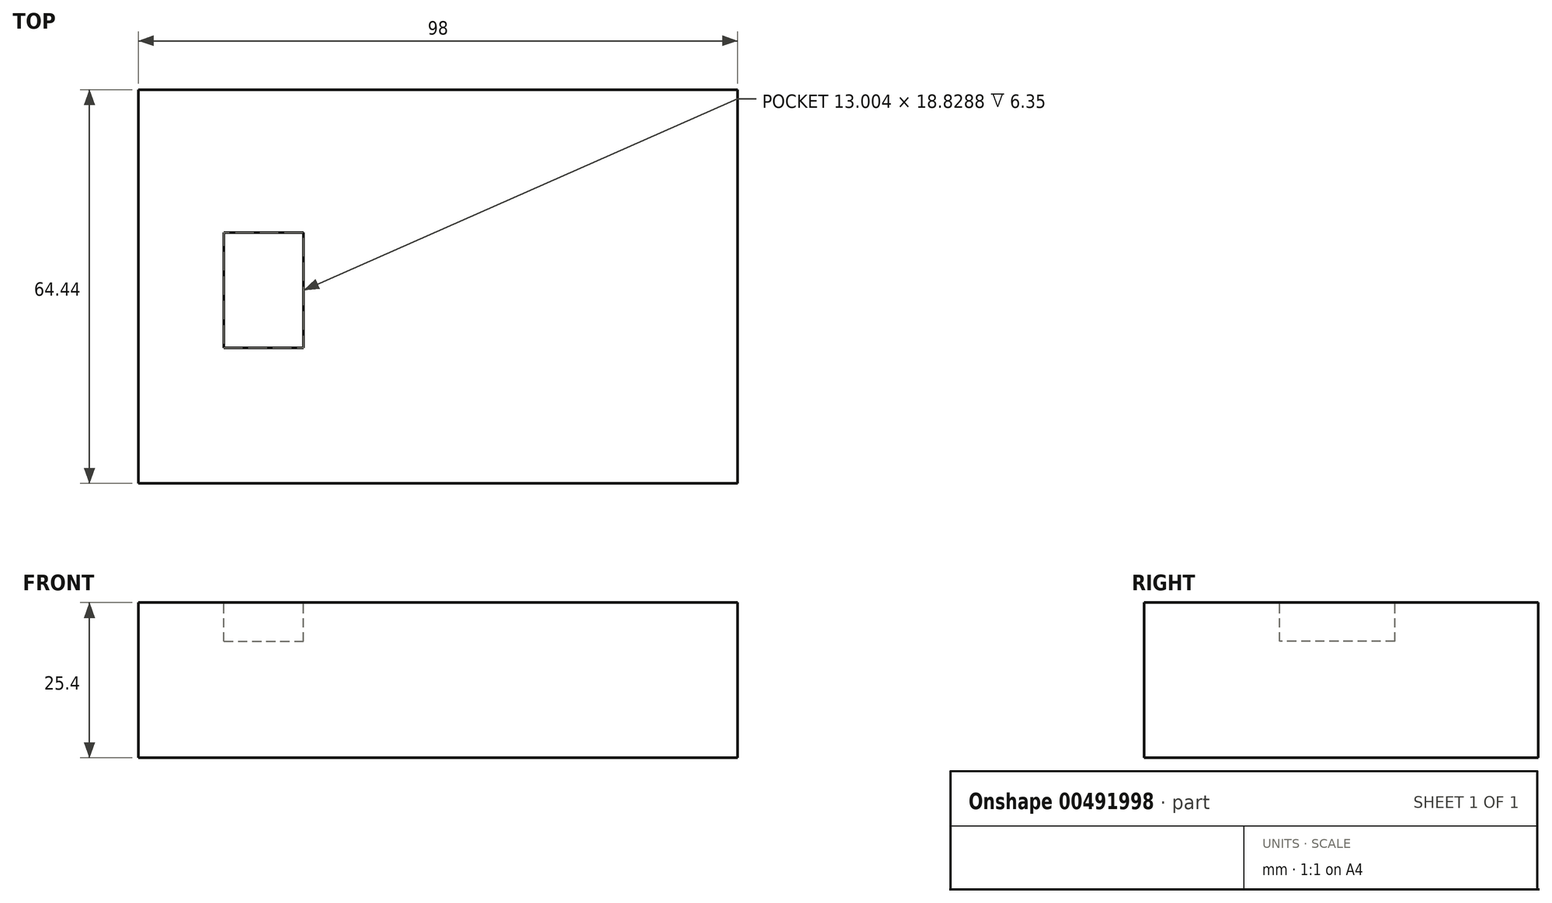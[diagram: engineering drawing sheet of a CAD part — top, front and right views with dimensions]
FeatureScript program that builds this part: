
annotation { "Feature Type Name" : "Feature", "Feature Type Description" : "" }
export const myFeature = defineFeature(function(context is Context, id is Id, definition is map)
    precondition{}
    {
        {
            var Q0;
            Q0=qCreatedBy(makeId("Top.planeOp"),FACE);
            var sketch = newSketch(context, id + "F0", { "sketchPlane" : qUnion([Q0])});
            skLineSegment(sketch, "E0.bottom", {"start": v(-49, -32.22) * mm, "end": v(49, -32.22) * mm});
            skLineSegment(sketch, "E0.top", {"start": v(-49, 32.22) * mm, "end": v(49, 32.22) * mm});
            skLineSegment(sketch, "E0.left", {"start": v(-49, -32.22) * mm, "end": v(-49, 32.22) * mm});
            skLineSegment(sketch, "E0.right", {"start": v(49, -32.22) * mm, "end": v(49, 32.22) * mm});
            skPoint(sketch, "E0.middle", {"position": v(0, 0) * mm});
            skLineSegment(sketch, "E1.bottom", {"start": v(25, 32.22) * mm, "end": v(-25, 32.22) * mm});
            skLineSegment(sketch, "E1.top", {"start": v(25, 32.22) * mm, "end": v(-25, 32.22) * mm});
            skLineSegment(sketch, "E1.left", {"start": v(25, 32.22) * mm, "end": v(25, 32.22) * mm});
            skLineSegment(sketch, "E1.right", {"start": v(-25, 32.22) * mm, "end": v(-25, 32.22) * mm});
            skPoint(sketch, "E1.middle", {"position": v(0, 32.22) * mm});
            skSolve(sketch);
        }
        {
            var Q0;
            Q0=makeQuery(id+"F0.imprint","IMPRINT",FACE,{"disambiguationData":[TD([[makeQuery(id+"F0.imprint","IMPRINT",EDGE,{"derivedFrom":sQuery(id+"F0.wireOp",EDGE,"E0.bottom")}),1.0]])]});
            extrude(context, id + "F1", {"entities" : qUnion([Q0]), "depth" : 25.4 * mm});
        }
        {
            var Q0;
            Q0=makeQuery(id+"F1.opExtrude","CAP_FACE",FACE,{"disambiguationData":[OSD([sQuery(id+"F0.wireOp",EDGE,"E0.bottom"),sQuery(id+"F0.wireOp",EDGE,"E0.top"),sQuery(id+"F0.wireOp",EDGE,"E0.left"),sQuery(id+"F0.wireOp",EDGE,"E0.right"),sQuery(id+"F0.wireOp",EDGE,"E1.top")])],"isStart":false});
            var sketch = newSketch(context, id + "F2", { "sketchPlane" : qUnion([Q0])});
            skLineSegment(sketch, "E2.bottom", {"start": v(-35, 8.8) * mm, "end": v(-22, 8.8) * mm});
            skLineSegment(sketch, "E2.top", {"start": v(-35, -10.03) * mm, "end": v(-22, -10.03) * mm});
            skLineSegment(sketch, "E2.left", {"start": v(-35, 8.8) * mm, "end": v(-35, -10.03) * mm});
            skLineSegment(sketch, "E2.right", {"start": v(-22, 8.8) * mm, "end": v(-22, -10.03) * mm});
            skSolve(sketch);
        }
        {
            var Q0;
            Q0=makeQuery(id+"F2.imprint","IMPRINT",FACE,{"disambiguationData":[TD([[makeQuery(id+"F2.imprint","IMPRINT",EDGE,{"derivedFrom":sQuery(id+"F2.wireOp",EDGE,"E2.bottom")}),-1.0]])]});
            extrude(context, id + "F3", {"entities" : qUnion([Q0]), "operationType" : NewBodyOperationType.REMOVE, "oppositeDirection" : true, "depth" : 6.35 * mm});
        }
    });
